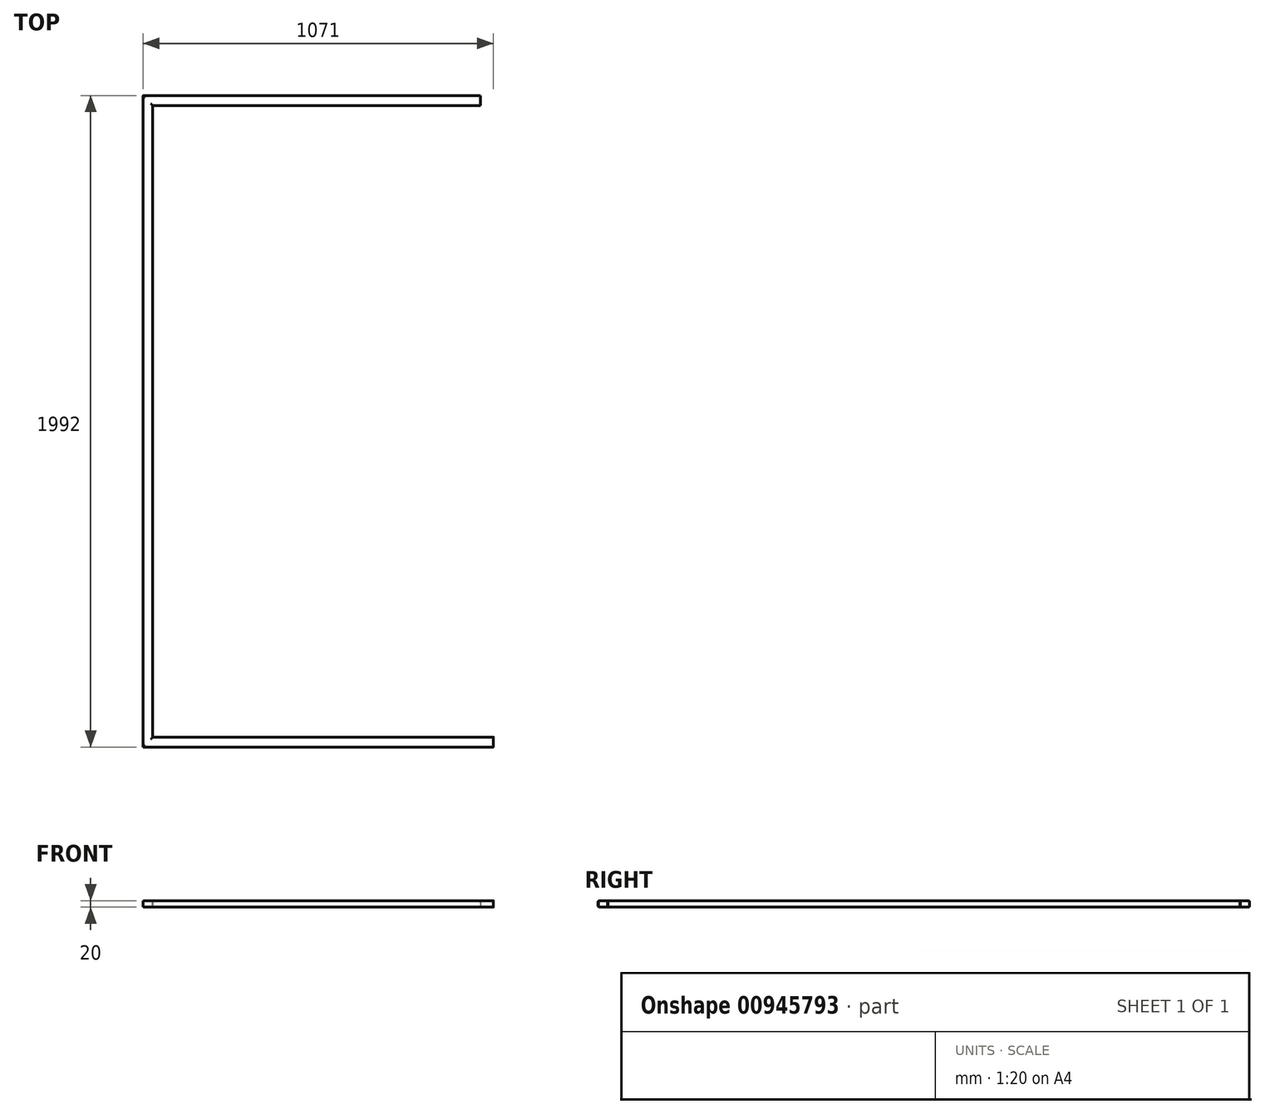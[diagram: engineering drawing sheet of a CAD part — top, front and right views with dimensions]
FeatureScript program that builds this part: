
annotation { "Feature Type Name" : "Feature", "Feature Type Description" : "" }
export const myFeature = defineFeature(function(context is Context, id is Id, definition is map)
    precondition{}
    {
        {
            var Q0;
            Q0=qCreatedBy(makeId("Right.planeOp"),FACE);
            var sketch = newSketch(context, id + "F0", { "sketchPlane" : qUnion([Q0])});
            skLineSegment(sketch, "E0.bottom", {"start": v(10, 10) * mm, "end": v(-10, 10) * mm});
            skLineSegment(sketch, "E0.top", {"start": v(10, -10) * mm, "end": v(-10, -10) * mm});
            skLineSegment(sketch, "E0.left", {"start": v(15, 5) * mm, "end": v(15, -5) * mm});
            skLineSegment(sketch, "E0.right", {"start": v(-15, 5) * mm, "end": v(-15, -5) * mm});
            skPoint(sketch, "E0.middle", {"position": v(0, 0) * mm});
            skPoint(sketch, "E1.visualSharp", {"position": v(-15, -10) * mm});
            skArc(sketch, "E1.filletArc", {"start": v(-15, -5) * mm, "mid": v(-13.54, -8.54) * mm, "end": v(-10, -10) * mm});
            skPoint(sketch, "E2.visualSharp", {"position": v(-15, 10) * mm});
            skArc(sketch, "E2.filletArc", {"start": v(-10, 10) * mm, "mid": v(-13.54, 8.54) * mm, "end": v(-15, 5) * mm});
            skPoint(sketch, "E3.visualSharp", {"position": v(15, 10) * mm});
            skArc(sketch, "E3.filletArc", {"start": v(15, 5) * mm, "mid": v(13.54, 8.54) * mm, "end": v(10, 10) * mm});
            skPoint(sketch, "E4.visualSharp", {"position": v(15, -10) * mm});
            skArc(sketch, "E4.filletArc", {"start": v(10, -10) * mm, "mid": v(13.54, -8.54) * mm, "end": v(15, -5) * mm});
            skArc(sketch, "E5.0", {"start": v(14, 5) * mm, "mid": v(12.83, 7.83) * mm, "end": v(10, 9) * mm});
            skLineSegment(sketch, "E5.1", {"start": v(14, 5) * mm, "end": v(14, -5) * mm});
            skLineSegment(sketch, "E5.2", {"start": v(10, 9) * mm, "end": v(-10, 9) * mm});
            skArc(sketch, "E5.3", {"start": v(10, -9) * mm, "mid": v(12.83, -7.83) * mm, "end": v(14, -5) * mm});
            skArc(sketch, "E5.4", {"start": v(-10, 9) * mm, "mid": v(-12.83, 7.83) * mm, "end": v(-14, 5) * mm});
            skLineSegment(sketch, "E5.5", {"start": v(-14, 5) * mm, "end": v(-14, -5) * mm});
            skArc(sketch, "E5.6", {"start": v(-14, -5) * mm, "mid": v(-12.83, -7.83) * mm, "end": v(-10, -9) * mm});
            skLineSegment(sketch, "E5.7", {"start": v(10, -9) * mm, "end": v(-10, -9) * mm});
            skSolve(sketch);
        }
        {
            var Q0;
            Q0=qCreatedBy(makeId("Top.planeOp"),FACE);
            var sketch = newSketch(context, id + "F1", { "sketchPlane" : qUnion([Q0])});
            skLineSegment(sketch, "E6", {"start": v(0, 0) * mm, "end": v(-1056, 0) * mm});
            skLineSegment(sketch, "E7", {"start": v(-1056, 0) * mm, "end": v(-1056, 1962) * mm});
            skLineSegment(sketch, "E8", {"start": v(-1056, 1962) * mm, "end": v(-40, 1962) * mm});
            skSolve(sketch);
        }
        {
            var Q0;
            Q0=makeQuery(id+"F0.imprint","IMPRINT",FACE,{"disambiguationData":[TD([[makeQuery(id+"F0.imprint","IMPRINT",EDGE,{"derivedFrom":sQuery(id+"F0.wireOp",EDGE,"E0.bottom")}),1.0]])]});
            var Q1;
            Q1=sQuery(id+"F1.wireOp",EDGE,"E6");
            var Q2;
            Q2=sQuery(id+"F1.wireOp",EDGE,"E7");
            var Q3;
            Q3=sQuery(id+"F1.wireOp",EDGE,"E8");
            sweep(context, id + "F2", {"profiles" : qUnion([Q0]), "path" : qUnion([Q1, Q2, Q3])});
        }
    });
